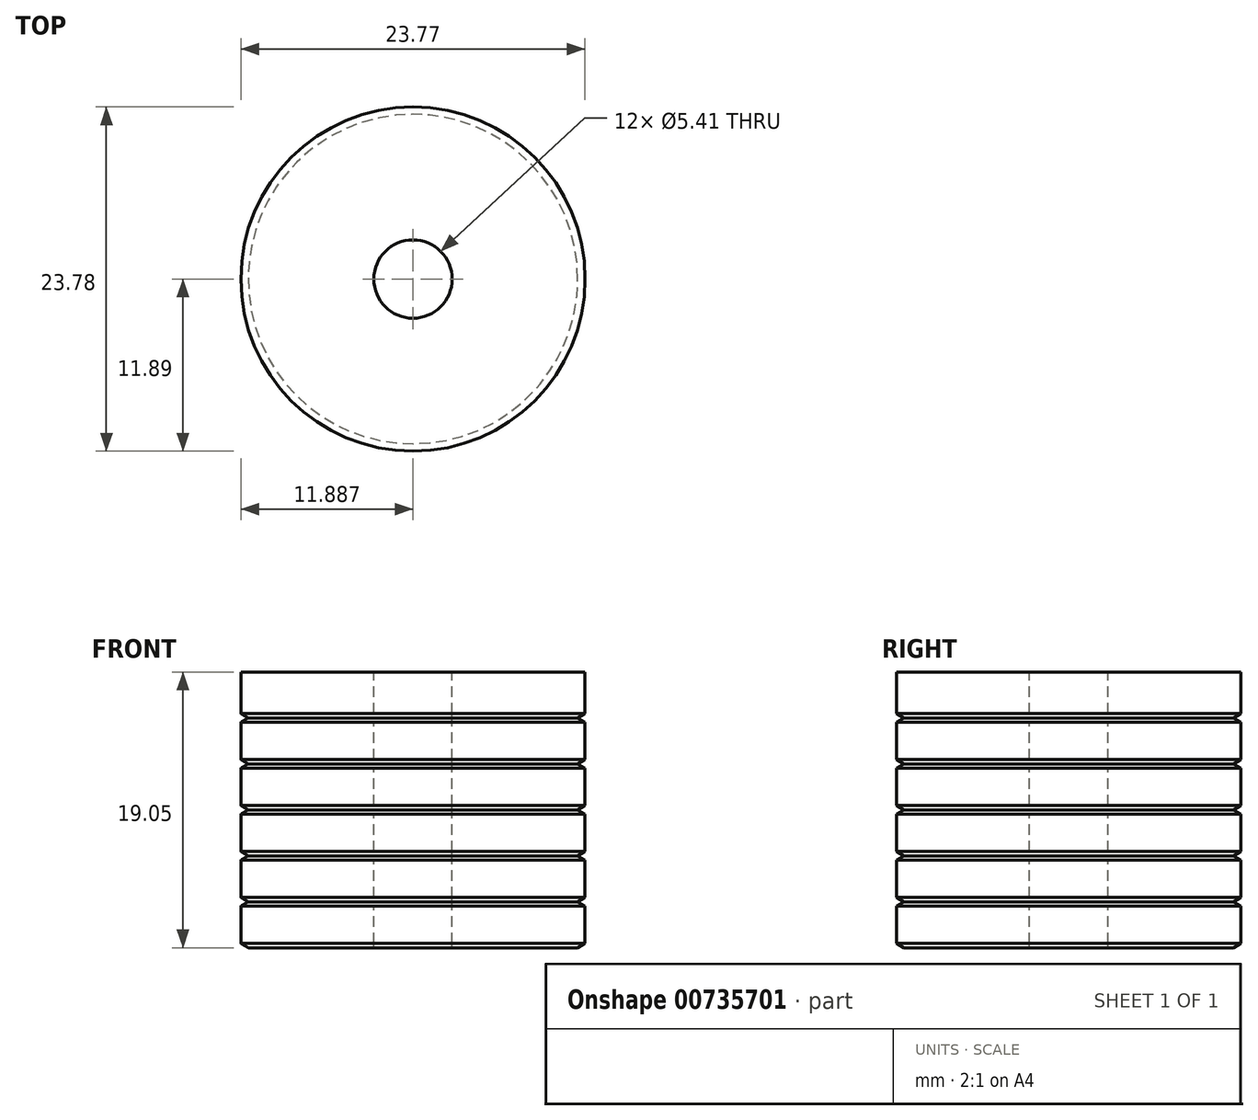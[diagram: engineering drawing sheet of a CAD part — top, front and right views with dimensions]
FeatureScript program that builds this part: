
annotation { "Feature Type Name" : "Feature", "Feature Type Description" : "" }
export const myFeature = defineFeature(function(context is Context, id is Id, definition is map)
    precondition{}
    {
        {
            var Q0;
            Q0=qCreatedBy(makeId("Front.planeOp"),FACE);
            var sketch = newSketch(context, id + "F0", { "sketchPlane" : qUnion([Q0])});
            skLineSegment(sketch, "E0.bottom", {"start": v(0, 0) * mm, "end": v(11.89, 0) * mm});
            skLineSegment(sketch, "E0.top", {"start": v(0, 19.05) * mm, "end": v(11.89, 19.05) * mm});
            skLineSegment(sketch, "E0.left", {"start": v(0, 0) * mm, "end": v(0, 19.05) * mm});
            skLineSegment(sketch, "E1", {"start": v(11.89, 3.18) * mm, "end": v(0.5, 3.18) * mm});
            skLineSegment(sketch, "E2", {"start": v(11.89, 6.35) * mm, "end": v(0.5, 6.35) * mm});
            skLineSegment(sketch, "E3", {"start": v(11.89, 9.53) * mm, "end": v(0.5, 9.53) * mm});
            skLineSegment(sketch, "E4", {"start": v(11.89, 12.7) * mm, "end": v(0.5, 12.7) * mm});
            skLineSegment(sketch, "E5", {"start": v(11.89, 15.88) * mm, "end": v(0.5, 15.88) * mm});
            skPoint(sketch, "E6", {"position": v(0.5, 15.87) * mm});
            skLineSegment(sketch, "E7", {"start": v(0.5, 15.87) * mm, "end": v(0, 16.17) * mm});
            skLineSegment(sketch, "E8", {"start": v(0.5, 15.88) * mm, "end": v(0, 15.58) * mm});
            skPoint(sketch, "E9.orphan", {"position": v(0, 15.88) * mm});
            skLineSegment(sketch, "E10", {"start": v(0, 16.17) * mm, "end": v(11.89, 16.17) * mm});
            skLineSegment(sketch, "E11", {"start": v(0, 15.58) * mm, "end": v(11.89, 15.58) * mm});
            skPoint(sketch, "E12", {"position": v(0.5, 6.35) * mm});
            skPoint(sketch, "E13", {"position": v(0.5, 3.17) * mm});
            skPoint(sketch, "E14", {"position": v(0.5, 0) * mm});
            skPoint(sketch, "E15", {"position": v(0.5, 9.53) * mm});
            skPoint(sketch, "E16", {"position": v(0.5, 12.7) * mm});
            skLineSegment(sketch, "E17", {"start": v(0.5, 12.7) * mm, "end": v(0, 13) * mm});
            skLineSegment(sketch, "E18", {"start": v(0.5, 12.7) * mm, "end": v(0, 12.4) * mm});
            skLineSegment(sketch, "E19", {"start": v(0.5, 9.53) * mm, "end": v(0, 9.82) * mm});
            skLineSegment(sketch, "E20", {"start": v(0.5, 9.53) * mm, "end": v(0, 9.23) * mm});
            skLineSegment(sketch, "E21", {"start": v(0.5, 6.35) * mm, "end": v(0, 6.64) * mm});
            skLineSegment(sketch, "E22", {"start": v(0.5, 6.35) * mm, "end": v(0, 6.06) * mm});
            skLineSegment(sketch, "E23", {"start": v(0.5, 3.17) * mm, "end": v(0, 3.47) * mm});
            skLineSegment(sketch, "E24", {"start": v(0.5, 3.17) * mm, "end": v(0, 2.88) * mm});
            skLineSegment(sketch, "E25", {"start": v(0.5, 0) * mm, "end": v(0, 0.3) * mm});
            skLineSegment(sketch, "E26", {"start": v(0, 13) * mm, "end": v(11.89, 13) * mm});
            skLineSegment(sketch, "E27", {"start": v(0, 12.4) * mm, "end": v(11.89, 12.4) * mm});
            skLineSegment(sketch, "E28", {"start": v(0, 9.82) * mm, "end": v(11.89, 9.82) * mm});
            skLineSegment(sketch, "E29", {"start": v(0, 9.23) * mm, "end": v(11.89, 9.23) * mm});
            skLineSegment(sketch, "E30", {"start": v(0, 6.64) * mm, "end": v(11.89, 6.64) * mm});
            skLineSegment(sketch, "E31", {"start": v(0, 6.06) * mm, "end": v(11.89, 6.06) * mm});
            skLineSegment(sketch, "E32", {"start": v(0, 3.47) * mm, "end": v(11.89, 3.47) * mm});
            skLineSegment(sketch, "E33", {"start": v(0, 2.88) * mm, "end": v(11.89, 2.88) * mm});
            skPoint(sketch, "E34.orphan", {"position": v(0, 12.7) * mm});
            skPoint(sketch, "E35.orphan", {"position": v(0, 9.53) * mm});
            skLineSegment(sketch, "E36", {"start": v(0, 0.3) * mm, "end": v(11.89, 0.3) * mm});
            skLineSegment(sketch, "E37", {"start": v(11.89, 19.05) * mm, "end": v(11.89, 0) * mm});
            skSolve(sketch);
        }
        {
            var Q0;
            {var subQ0=sQuery(id+"F0.wireOp",EDGE,"E0.top");Q0=makeQuery(id+"F0.imprint","IMPRINT",FACE,{"disambiguationData":[TD([[makeQuery(id+"F0.imprint","IMPRINT",EDGE,{"derivedFrom":subQ0}),-1.0]])]});}
            var Q1;
            {var subQ0=sQuery(id+"F0.wireOp",EDGE,"E11");Q1=makeQuery(id+"F0.imprint","IMPRINT",FACE,{"disambiguationData":[TD([[makeQuery(id+"F0.imprint","IMPRINT",EDGE,{"derivedFrom":subQ0}),-1.0]])]});}
            var Q2;
            {var subQ0=sQuery(id+"F0.wireOp",EDGE,"E27");Q2=makeQuery(id+"F0.imprint","IMPRINT",FACE,{"disambiguationData":[TD([[makeQuery(id+"F0.imprint","IMPRINT",EDGE,{"derivedFrom":subQ0}),-1.0]])]});}
            var Q3;
            {var subQ0=sQuery(id+"F0.wireOp",EDGE,"E29");Q3=makeQuery(id+"F0.imprint","IMPRINT",FACE,{"disambiguationData":[TD([[makeQuery(id+"F0.imprint","IMPRINT",EDGE,{"derivedFrom":subQ0}),-1.0]])]});}
            var Q4;
            {var subQ0=sQuery(id+"F0.wireOp",EDGE,"E31");Q4=makeQuery(id+"F0.imprint","IMPRINT",FACE,{"disambiguationData":[TD([[makeQuery(id+"F0.imprint","IMPRINT",EDGE,{"derivedFrom":subQ0}),-1.0]])]});}
            var Q5;
            {var subQ0=sQuery(id+"F0.wireOp",EDGE,"E33");Q5=makeQuery(id+"F0.imprint","IMPRINT",FACE,{"disambiguationData":[TD([[makeQuery(id+"F0.imprint","IMPRINT",EDGE,{"derivedFrom":subQ0}),-1.0]])]});}
            var Q6;
            Q6=sQuery(id+"F0.wireOp",EDGE,"E37");
            revolve(context, id + "F1", {"surfaceOperationType" : NewSurfaceOperationType.NEW, "entities" : qUnion([Q0, Q1, Q2, Q3, Q4, Q5]), "axis" : qUnion([Q6]), "revolveType" : RevolveType.FULL});
        }
        {
            var Q0;
            {var subQ0=sQuery(id+"F0.wireOp",EDGE,"E5");Q0=makeQuery(id+"F0.imprint","IMPRINT",FACE,{"disambiguationData":[TD([[makeQuery(id+"F0.imprint","IMPRINT",EDGE,{"derivedFrom":subQ0}),-1.0]])]});}
            var Q1;
            {var subQ0=sQuery(id+"F0.wireOp",EDGE,"E5");Q1=makeQuery(id+"F0.imprint","IMPRINT",FACE,{"disambiguationData":[TD([[makeQuery(id+"F0.imprint","IMPRINT",EDGE,{"derivedFrom":subQ0}),1.0]])]});}
            var Q2;
            {var subQ0=sQuery(id+"F0.wireOp",EDGE,"E4");Q2=makeQuery(id+"F0.imprint","IMPRINT",FACE,{"disambiguationData":[TD([[makeQuery(id+"F0.imprint","IMPRINT",EDGE,{"derivedFrom":subQ0}),-1.0]])]});}
            var Q3;
            {var subQ0=sQuery(id+"F0.wireOp",EDGE,"E4");Q3=makeQuery(id+"F0.imprint","IMPRINT",FACE,{"disambiguationData":[TD([[makeQuery(id+"F0.imprint","IMPRINT",EDGE,{"derivedFrom":subQ0}),1.0]])]});}
            var Q4;
            {var subQ0=sQuery(id+"F0.wireOp",EDGE,"E3");Q4=makeQuery(id+"F0.imprint","IMPRINT",FACE,{"disambiguationData":[TD([[makeQuery(id+"F0.imprint","IMPRINT",EDGE,{"derivedFrom":subQ0}),-1.0]])]});}
            var Q5;
            {var subQ0=sQuery(id+"F0.wireOp",EDGE,"E3");Q5=makeQuery(id+"F0.imprint","IMPRINT",FACE,{"disambiguationData":[TD([[makeQuery(id+"F0.imprint","IMPRINT",EDGE,{"derivedFrom":subQ0}),1.0]])]});}
            var Q6;
            {var subQ0=sQuery(id+"F0.wireOp",EDGE,"E2");Q6=makeQuery(id+"F0.imprint","IMPRINT",FACE,{"disambiguationData":[TD([[makeQuery(id+"F0.imprint","IMPRINT",EDGE,{"derivedFrom":subQ0}),-1.0]])]});}
            var Q7;
            {var subQ0=sQuery(id+"F0.wireOp",EDGE,"E2");Q7=makeQuery(id+"F0.imprint","IMPRINT",FACE,{"disambiguationData":[TD([[makeQuery(id+"F0.imprint","IMPRINT",EDGE,{"derivedFrom":subQ0}),1.0]])]});}
            var Q8;
            {var subQ0=sQuery(id+"F0.wireOp",EDGE,"E1");Q8=makeQuery(id+"F0.imprint","IMPRINT",FACE,{"disambiguationData":[TD([[makeQuery(id+"F0.imprint","IMPRINT",EDGE,{"derivedFrom":subQ0}),-1.0]])]});}
            var Q9;
            {var subQ0=sQuery(id+"F0.wireOp",EDGE,"E1");Q9=makeQuery(id+"F0.imprint","IMPRINT",FACE,{"disambiguationData":[TD([[makeQuery(id+"F0.imprint","IMPRINT",EDGE,{"derivedFrom":subQ0}),1.0]])]});}
            var Q10;
            {var subQ3=sQuery(id+"F0.wireOp",EDGE,"E25");Q10=makeQuery(id+"F0.imprint","IMPRINT",FACE,{"disambiguationData":[TD([[makeQuery(id+"F0.imprint","IMPRINT",EDGE,{"derivedFrom":subQ3}),-1.0]])]});}
            var Q11;
            {var subQ0=sQuery(id+"F0.wireOp",EDGE,"E0.left");Q11=makeQuery(id+"F1.opRevolve","SWEPT_FACE",FACE,{"disambiguationData":[OSD([subQ0]),TDD([makeQuery(id+"F0.imprint","IMPRINT",EDGE,{"disambiguationData":[TD([[makeQuery(id+"F0.imprint","INTERSECT",VERTEX,{"derivedFrom":[subQ0,sQuery(id+"F0.wireOp",EDGE,"E8"),sQuery(id+"F0.wireOp",EDGE,"E11")]}),1.0]])],"derivedFrom":subQ0})])]});}
            revolve(context, id + "F2", {"surfaceOperationType" : NewSurfaceOperationType.NEW, "entities" : qUnion([Q0, Q1, Q2, Q3, Q4, Q5, Q6, Q7, Q8, Q9, Q10]), "axis" : qUnion([Q11]), "revolveType" : RevolveType.FULL});
        }
        {
            var Q0;
            Q0=makeQuery(id+"F1.opRevolve","SWEPT_FACE",FACE,{"disambiguationData":[OSD([sQuery(id+"F0.wireOp",EDGE,"E0.top")])]});
            var sketch = newSketch(context, id + "F3", { "sketchPlane" : qUnion([Q0])});
            skCircle(sketch, "E38", {"center": v(11.89, 0) * mm, "radius": 2.7 * mm});
            skSolve(sketch);
        }
        {
            var Q0;
            Q0=makeQuery(id+"F3.imprint","IMPRINT",FACE,{"disambiguationData":[TD([[makeQuery(id+"F3.imprint","IMPRINT",EDGE,{"derivedFrom":sQuery(id+"F3.wireOp",EDGE,"E38")}),1.0]])]});
            extrude(context, id + "F4", {"entities" : qUnion([Q0]), "operationType" : NewBodyOperationType.REMOVE, "oppositeDirection" : true, "depth" : 25.4 * mm, "offsetDistance" : 25.4 * mm});
        }
    });
